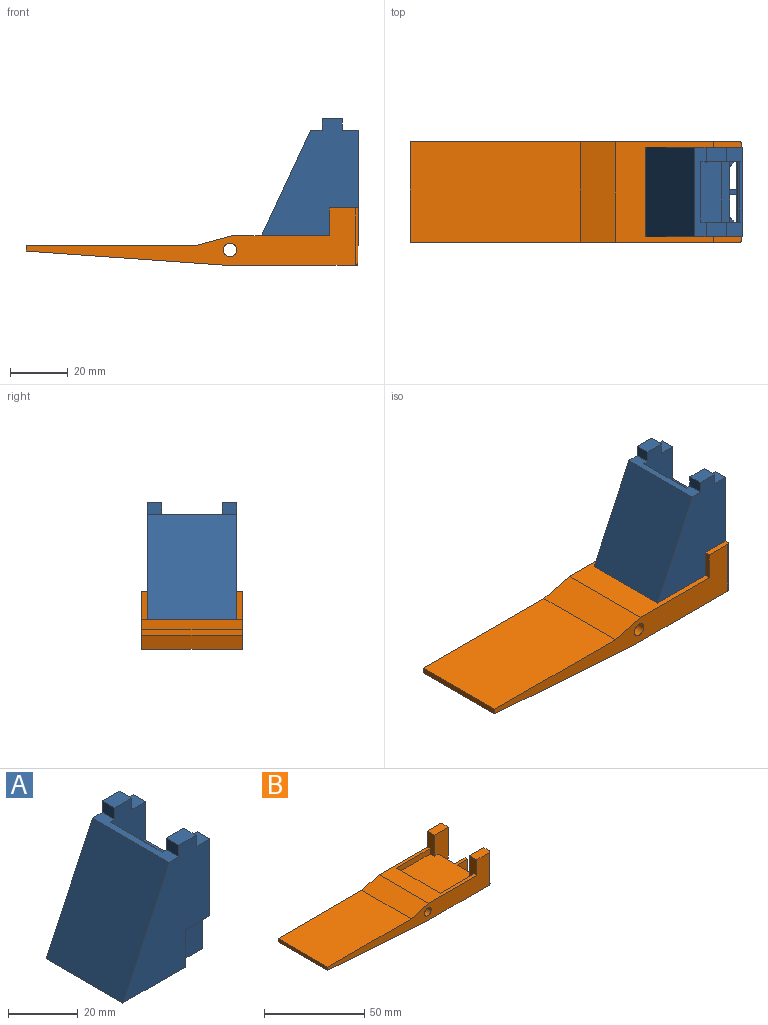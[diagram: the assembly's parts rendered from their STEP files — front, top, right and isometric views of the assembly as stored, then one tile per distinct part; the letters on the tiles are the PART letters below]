
ASSEMBLY  parts=2 mates=1
PART A: 49 faces, bbox 35.1x31x44 mm
  f0: plane 44x29.29mm, normal (0,-1,0), area 807.7mm2, adj f4,f6,f7,f9,f10,f13,f19,f20
  f1: plane 1.69x1.69mm, normal (0,0,1), area 1.4mm2, adj f3,f33,f46
  f2: plane 2.53x1.5mm, normal (0,0,1), area 3.8mm2, adj f29,f30,f42,f46
  f3: plane 44x29.29mm, normal (0,1,0), area 806.6mm2, adj f1,f4,f5,f7,f9,f10,f13,f24
  f4: plane 25x9.89mm, normal (0,0,-1), area 146.4mm2, adj f0,f3,f8,f9,f12,f28,f29,f30
  f5: plane 5.48x5mm, normal (0,0,1), area 27.4mm2, adj f3,f9,f17,f25
  f6: plane 5.48x5mm, normal (0,0,1), area 27.4mm2, adj f0,f9,f16,f22
  f7: plane 21.85x21mm, normal (0.09,0,1), area 460.4mm2, adj f0,f3,f18,f19,f20,f27,f35
  f8: plane 12.96x9.91mm, normal (0,1,0), area 128.4mm2, adj f4,f9,f14,f15,f39
  f9: plane 40x31mm, normal (1,0,0), area 647.1mm2, adj f0,f3,f4,f5,f6,f8,f12,f14
  f10: plane 31x4mm, normal (0,0,1), area 86.3mm2, adj f0,f3,f11,f13,f16,f17,f21,f24
  f11: plane 40x31mm, normal (-0.91,0,0.42), area 1368.2mm2, adj f10,f16,f17,f37
  f12: plane 13x9.91mm, normal (0,-1,0), area 128.9mm2, adj f4,f9,f15,f36,f39
  f13: plane 32.2x21mm, normal (0.91,0,-0.42), area 746.1mm2, adj f0,f3,f10,f35
  f14: plane 9.91x3mm, normal (0,0,-1), area 29.7mm2, adj f8,f9,f15,f16
  f15: plane 31x13mm, normal (1,0,0), area 77.9mm2, adj f8,f12,f14,f16,f17,f36,f37,f39
  f16: plane 44x35.13mm, normal (0,1,0), area 931.8mm2, adj f6,f9,f10,f11,f14,f15,f21,f22
  f17: plane 44x35.13mm, normal (0,-1,0), area 931.4mm2, adj f5,f9,f10,f11,f15,f24,f25,f26
  f18: plane 2.05x0.51mm, normal (0,1,0), area 1mm2, adj f7,f19,f20,f38
  f19: plane 2.01x0.3mm, normal (1,0,0), area 0.6mm2, adj f0,f7,f18,f38
  f20: plane 2.01x0.3mm, normal (-1,0,0), area 0.6mm2, adj f0,f7,f18,f38
  f21: plane 5x4mm, normal (-1,0,0), area 20mm2, adj f0,f10,f16,f23
  f22: plane 5x4mm, normal (1,0,0), area 20mm2, adj f0,f6,f16,f23
  f23: plane 7x5mm, normal (0,0,1), area 35mm2, adj f0,f16,f21,f22
  f24: plane 5x4mm, normal (-1,0,0), area 20mm2, adj f3,f10,f17,f26
  f25: plane 5x4mm, normal (1,0,0), area 20mm2, adj f3,f5,f17,f26
  f26: plane 7x5mm, normal (0,0,1), area 35mm2, adj f3,f17,f24,f25
  f27: plane 21x10.91mm, normal (-1,0,0), area 229.2mm2, adj f0,f3,f7,f47
  f28: plane 12x6.75mm, normal (1,0,0), area 81mm2, adj f4,f29,f33,f45
  f29: plane 12x5.64mm, normal (0,-1,0), area 67.7mm2, adj f2,f4,f9,f28,f40,f45
  f30: plane 12x5.64mm, normal (0,1,0), area 67.7mm2, adj f2,f4,f9,f31,f41,f48
  f31: plane 12x6.75mm, normal (1,0,0), area 81mm2, adj f4,f30,f34,f48
  f32: plane 1.69x1.69mm, normal (0,0,1), area 1.4mm2, adj f0,f34,f46
  f33: plane 12x3mm, normal (0.71,0.71,0), area 50.9mm2, adj f1,f3,f4,f28,f45
  f34: plane 12x3mm, normal (0.71,-0.71,0), area 50.9mm2, adj f0,f4,f31,f32,f48
  f35: plane 21x3.8mm, normal (1,0,0.08), area 80mm2, adj f0,f3,f7,f13
  f36: plane 9.91x3mm, normal (0,0,-1), area 29.7mm2, adj f9,f12,f15,f17
  f37: plane 31x25.22mm, normal (0,0,-1), area 781.8mm2, adj f11,f15,f16,f17
  f38: plane 0.51x0.3mm, normal (0.09,0,1), area 0.2mm2, adj f0,f18,f19,f20
  f39: plane 25x0.02mm, normal (-0.02,0,-1), area 0.5mm2, adj f4,f8,f12,f15
  f40: plane 9.75x1.8mm, normal (0,0,-1), area 17.6mm2, adj f3,f9,f29,f42
  f41: plane 9.75x1.8mm, normal (0,0,-1), area 17.6mm2, adj f0,f9,f30,f42
  f42: plane 21x13.62mm, normal (-1,0,0), area 285.9mm2, adj f0,f2,f3,f40,f41,f43
  f43: cylinder r=1mm len=21mm, axis (0,-1,0), area 33mm2, adj f0,f3,f42,f44
  f44: plane 21x0.8mm, normal (0,0,1), area 16.8mm2, adj f0,f3,f9,f43
  f45: plane 8.07x1.32mm, normal (0,0,-1), area 9.7mm2, adj f28,f29,f33,f46
  f46: plane 21x1mm, normal (1,0,0), area 21mm2, adj f0,f1,f2,f3,f32,f45,f47,f48
  f47: plane 21x2.82mm, normal (0,0,1), area 59.1mm2, adj f0,f3,f27,f46
  f48: plane 8.07x1.32mm, normal (0,0,-1), area 9.7mm2, adj f30,f31,f34,f46
PART B: 32 faces, bbox 115.4x35x19.9 mm
  f0: plane 35x33.93mm, normal (0,0,1), area 453.4mm2, adj f6,f9,f10,f16,f17,f23,f24,f25
  f1: plane 18.9x9.91mm, normal (0,-1,0), area 170.8mm2, adj f4,f9,f14,f19,f22,f31
  f2: plane 18.9x9.91mm, normal (0,1,0), area 170.8mm2, adj f3,f5,f6,f21,f22,f26
  f3: plane 9.91x5mm, normal (0,0,1), area 49.4mm2, adj f2,f5,f6,f17,f27
  f4: plane 18.9x4mm, normal (1,0,0), area 75.6mm2, adj f1,f14,f29,f30
  f5: plane 18.9x4mm, normal (1,0,0), area 75.6mm2, adj f2,f3,f27,f28
  f6: plane 13x5mm, normal (-1,0,0), area 58.4mm2, adj f0,f2,f3,f17,f22,f24
  f7: plane 46.13x35mm, normal (0,0,-1), area 1425.4mm2, adj f8,f13,f16,f17,f18,f19,f20,f21
  f8: plane 6.9x1.5mm, normal (1,0,0), area 10.4mm2, adj f7,f18,f20,f22
  f9: plane 13x5mm, normal (-1,0,0), area 58.4mm2, adj f0,f1,f14,f16,f22,f25
  f10: plane 35x12.38mm, normal (-0.26,0,0.97), area 448.6mm2, adj f0,f11,f16,f17
  f11: plane 59.17x35mm, normal (0,0,1), area 2070.8mm2, adj f10,f12,f16,f17
  f12: plane 35x2mm, normal (-1,0,0), area 70mm2, adj f11,f13,f16,f17
  f13: plane 69.27x35mm, normal (-0.07,0,-1), area 2430.3mm2, adj f7,f12,f16,f17
  f14: plane 9.91x5mm, normal (0,0,1), area 49.4mm2, adj f1,f4,f9,f16,f29
  f15: cylinder r=2.35mm len=35mm, axis (0,-1,0), area 516.8mm2, adj f16,f17
  f16: plane 114.39x19.9mm, normal (0,1,0), area 850.6mm2, adj f0,f7,f9,f10,f11,f12,f13,f14
  f17: plane 114.39x19.9mm, normal (0,-1,0), area 850.6mm2, adj f0,f3,f6,f7,f10,f11,f12,f13
  f18: plane 7.1x6.9mm, normal (0,1,0), area 49mm2, adj f7,f8,f19,f22
  f19: plane 12.75x6.9mm, normal (1,0,0), area 81.3mm2, adj f1,f7,f18,f22,f31
  f20: plane 7.1x6.9mm, normal (0,-1,0), area 49mm2, adj f7,f8,f21,f22
  f21: plane 12.75x6.9mm, normal (1,0,0), area 81.3mm2, adj f2,f7,f20,f22,f26
  f22: plane 35.13x31mm, normal (0,0,1), area 862.8mm2, adj f1,f2,f6,f8,f9,f18,f19,f20
  f23: plane 31x3.3mm, normal (0.91,0,-0.42), area 112.8mm2, adj f0,f22,f24,f25
  f24: plane 25.22x3.3mm, normal (0,1,0), area 80.6mm2, adj f0,f6,f22,f23
  f25: plane 25.22x3.3mm, normal (0,-1,0), area 80.6mm2, adj f0,f9,f22,f23
  f26: cylinder r=1mm len=7.1mm, axis (-1,0,0), area 10.6mm2, adj f2,f7,f21,f28
  f27: cylinder r=1mm len=19.9mm, axis (0,0,1), area 30.7mm2, adj f3,f5,f17,f28
  f28: cylinder r=1mm len=5mm, axis (0,1,0), area 6.7mm2, adj f5,f7,f26,f27
  f29: cylinder r=1mm len=19.9mm, axis (0,0,-1), area 30.7mm2, adj f4,f14,f16,f30
  f30: cylinder r=1mm len=5mm, axis (0,1,0), area 6.7mm2, adj f4,f7,f29,f31
  f31: cylinder r=1mm len=7.1mm, axis (1,0,0), area 10.6mm2, adj f1,f7,f19,f30
PLACE A t=(50.76,-0.9,5.68)mm
PLACE B t=(50.76,-43.43,15.68)mm
MATE fastened A.f37 <-> B.f22  axis (0,0,-1) through (13.63,-25.93,-33.42)mm
